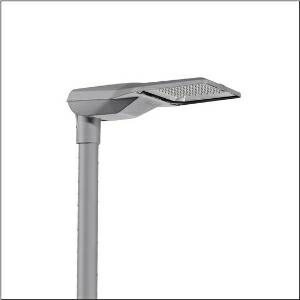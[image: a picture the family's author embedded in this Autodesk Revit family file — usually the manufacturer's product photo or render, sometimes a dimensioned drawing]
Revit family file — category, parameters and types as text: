
# Revit family: streetlight_sl_21_iq_midi___stw1_0a_5xe3e21d08nb_941d
name_source: partatom
category: Lighting Fixtures
units: mm (PartAtom-declared; Revit-internal decimal feet)

## family parameters
Cut with Voids When Loaded = No
Host = Face
Light Source = No
Part Type = Normal
Room Calculation Point = No
Round Connector Dimension = Use Diameter
Shared = No

## types (1)
- --- (1 x LED, 19210 lm, 155.5 W, 2200K)
    Apparent Load = 155 VA
    CIE Flux Codes = 39 75 98 100 100
    Color Rendering = 70
    Color Temperature = 2200K
    Default Elevation = 1800 mm
    Description = Streetlight SL 21 iQ midi, mast luminaire, primary light control with lens, of PMMA, primary optical cover: cover, of toughened safety glass, transparent, light distribution: STW1.0a, light emission: direct distribution, primary light characteristic: asymmetric, installation type: post-top, side-entry, LED, High Power LED, rated luminous flux: 19.210lm, luminous efficacy: 124lm/W, light colour: 722, colour temperature: 2200K, control gear: iQ-Comfort, control: Auto-Match, Temp-Guard, Lumen-Switch, Night-Set, Smart-Wire, Light-Fading, Desk-Remote (wireless, voltage-free reading and setting of iQ features in the workshop via application-optimized NFC function/RFID function), optimised constant luminous flux control (CLO 2.0), pre-setting: linear dimming characteristic, mains connection: 230..240V, AC, 50/60Hz, start of lifetime: 156W, end of service life: 162W, reduction: 69W, luminaire housing, of diecast aluminium, powder-coated, SITECO metallic grey (DB 702S), corrosivity category C5 high according to DIN EN ISO 12944, please order mast flange separately, inclination adjustable: 0°, 5°, 10°, 15°, sealing non-destructively replaceable, multi-level sealing system, length: 644mm, width: 335mm, height: 110mm, mast flange for spigot size: 42mm (side-entry): 5XC10008XM4, 60/48mm (side-entry/post-top): 5XC10108XM2, 76/60mm (side-entry/post-top): 5XC10108XM1, mounting height: 4..8m, protection rating (complete): IP66, insulation class (complete): insulation class II (safety insulation), certification: CE, ENEC, ENEC+, VDE, impact resistance: IK10, permissible operating ambient temperature for outdoor applications: -40..+50°C, standard-compliant lighting for roads and squares, packaging unit: 1 piece

Light Distribution: STW1.0a
    Height = 111 mm
    Lamp = 1 x LED
    Lamp Light Flux = 19210 lm
    Lamp Power = 155.5 W
    Lamp count = 1
    Length = 644 mm
    Luminous efficacy = 124 lm/W
    Manufacturer = Siteco
    ModVariant = No
    Model = 5XE3E21D08NB
    Number of Poles = 1
    OnlyDefault = Yes
    Power Factor = 1
    Product Name = Streetlight SL 21 iQ midi | STW1.0a
    Product group = mast luminaire | pylon top
    ProductGroupID = 6100
    Protection Class = Protection class II
    Protection Degree = IP 66
    RLX_Detail_Level = 1
    RLX_Emergency_Light_Flux = 0 lm
    RLX_Emergency_Type = 0
    RLX_Emergency_Type_DB = No
    RlxData = <blob elided: 27281 chars, md5=55ba9967>
    Socket = socket
    Standby Power = 0 W
    System Light Flux = 19210 lm
    System Power = 155 W
    Type Comments = factory setting: luminous flux: 100 % | dim-lin: 254 | 823 mA
    Type Image = l_1004298.jpg
    URL = http://relux.com
    VarID = @adj_169481
    Voltage = 0 V
    Weight = 0.00 kg
    Width = 336 mm

## geometry (parser evidence)
native form markers: Blend x4, Sweep x12
no freeform markers — native parametric forms only
